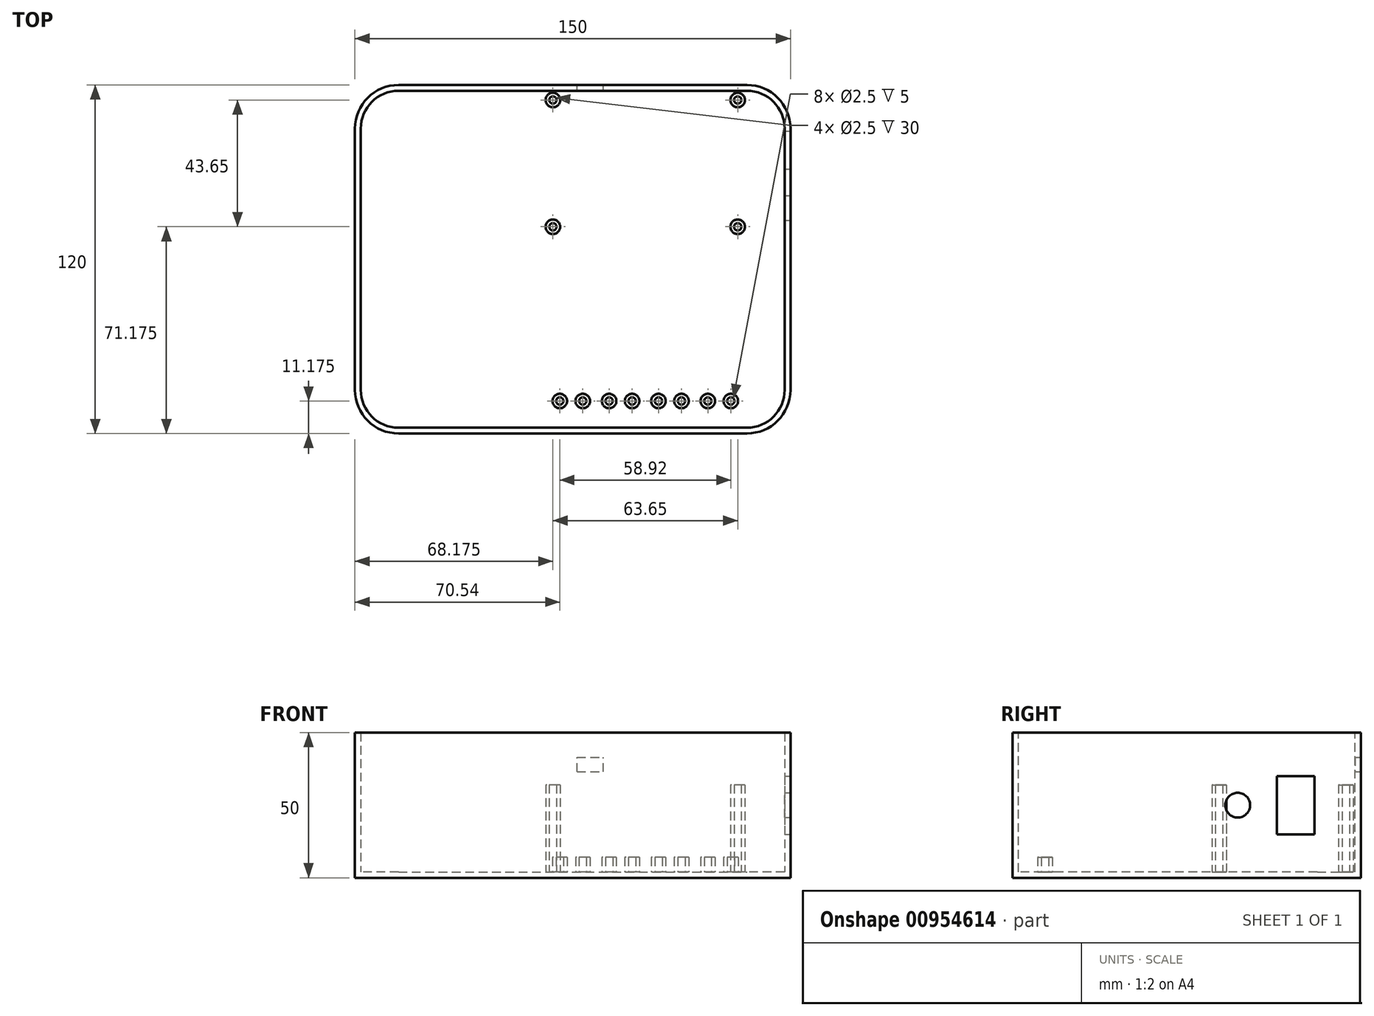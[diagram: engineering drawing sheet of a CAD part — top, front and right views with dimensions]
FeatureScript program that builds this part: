
annotation { "Feature Type Name" : "Feature", "Feature Type Description" : "" }
export const myFeature = defineFeature(function(context is Context, id is Id, definition is map)
    precondition{}
    {
        {
            var Q0;
            Q0=qCreatedBy(makeId("Top.planeOp"),FACE);
            var sketch = newSketch(context, id + "F0", { "sketchPlane" : qUnion([Q0])});
            skLineSegment(sketch, "E0.bottom", {"start": v(-60, 60) * mm, "end": v(60, 60) * mm});
            skLineSegment(sketch, "E0.top", {"start": v(-60, -60) * mm, "end": v(60, -60) * mm});
            skLineSegment(sketch, "E0.left", {"start": v(-75, 45) * mm, "end": v(-75, -45) * mm});
            skLineSegment(sketch, "E0.right", {"start": v(75, 45) * mm, "end": v(75, -45) * mm});
            skPoint(sketch, "E0.middle", {"position": v(0, 0) * mm});
            skPoint(sketch, "E1.visualSharp", {"position": v(-75, 60) * mm});
            skArc(sketch, "E1.filletArc", {"start": v(-60, 60) * mm, "mid": v(-70.6, 55.6) * mm, "end": v(-75, 45) * mm});
            skPoint(sketch, "E2.visualSharp", {"position": v(75, 60) * mm});
            skArc(sketch, "E2.filletArc", {"start": v(75, 45) * mm, "mid": v(70.6, 55.6) * mm, "end": v(60, 60) * mm});
            skPoint(sketch, "E3.visualSharp", {"position": v(75, -60) * mm});
            skArc(sketch, "E3.filletArc", {"start": v(60, -60) * mm, "mid": v(70.6, -55.6) * mm, "end": v(75, -45) * mm});
            skPoint(sketch, "E4.visualSharp", {"position": v(-75, -60) * mm});
            skArc(sketch, "E4.filletArc", {"start": v(-75, -45) * mm, "mid": v(-70.6, -55.6) * mm, "end": v(-60, -60) * mm});
            skSolve(sketch);
        }
        {
            var Q0;
            Q0=qSketchRegion(id+"F0",true);
            extrude(context, id + "F1", {"entities" : qUnion([Q0]), "depth" : 50 * mm, "offsetDistance" : 25 * mm});
        }
        {
            var Q0;
            Q0=makeQuery(id+"F1.opExtrude","CAP_FACE",FACE,{"disambiguationData":[OSD([sQuery(id+"F0.wireOp",EDGE,"E0.bottom"),sQuery(id+"F0.wireOp",EDGE,"E0.top"),sQuery(id+"F0.wireOp",EDGE,"E0.left"),sQuery(id+"F0.wireOp",EDGE,"E0.right"),sQuery(id+"F0.wireOp",EDGE,"E1.filletArc"),sQuery(id+"F0.wireOp",EDGE,"E2.filletArc"),sQuery(id+"F0.wireOp",EDGE,"E3.filletArc"),sQuery(id+"F0.wireOp",EDGE,"E4.filletArc")])],"isStart":false});
            shell(context, id + "F2", {"entities" : qUnion([Q0]), "thickness" : 2 * mm});
        }
        {
            var Q0;
            Q0=makeQuery(id+"F2.opShell","OFFSET_FACE",FACE,{"disambiguationData":[OSD([sQuery(id+"F0.wireOp",EDGE,"E0.bottom"),sQuery(id+"F0.wireOp",EDGE,"E0.top"),sQuery(id+"F0.wireOp",EDGE,"E0.left"),sQuery(id+"F0.wireOp",EDGE,"E0.right"),sQuery(id+"F0.wireOp",EDGE,"E1.filletArc"),sQuery(id+"F0.wireOp",EDGE,"E2.filletArc"),sQuery(id+"F0.wireOp",EDGE,"E3.filletArc"),sQuery(id+"F0.wireOp",EDGE,"E4.filletArc")])]});
            var sketch = newSketch(context, id + "F3", { "sketchPlane" : qUnion([Q0])});
            skCircle(sketch, "E5", {"center": v(-6.82, 54.82) * mm, "radius": 2.5 * mm});
            skCircle(sketch, "E6.MirrorC", {"center": v(-6.82, 11.17) * mm, "radius": 2.5 * mm});
            skCircle(sketch, "E7", {"center": v(56.83, 54.83) * mm, "radius": 2.5 * mm});
            skCircle(sketch, "E8.MirrorC", {"center": v(56.83, 11.17) * mm, "radius": 2.5 * mm});
            skCircle(sketch, "E9", {"center": v(-6.82, 54.82) * mm, "radius": 1.25 * mm});
            skCircle(sketch, "E10", {"center": v(56.83, 54.83) * mm, "radius": 1.25 * mm});
            skCircle(sketch, "E11", {"center": v(56.83, 11.17) * mm, "radius": 1.25 * mm});
            skCircle(sketch, "E12", {"center": v(-6.82, 11.17) * mm, "radius": 1.25 * mm});
            skSolve(sketch);
        }
        {
            var Q0;
            Q0=qSketchRegion(id+"F3",true);
            extrude(context, id + "F4", {"entities" : qUnion([Q0]), "operationType" : NewBodyOperationType.ADD, "depth" : 30 * mm, "offsetDistance" : 25 * mm});
        }
        {
            var Q0;
            Q0=makeQuery(id+"F1.opExtrude","SWEPT_FACE",FACE,{"disambiguationData":[OSD([sQuery(id+"F0.wireOp",EDGE,"E0.bottom")])]});
            var sketch = newSketch(context, id + "F5", { "sketchPlane" : qUnion([Q0])});
            skLineSegment(sketch, "E13.bottom", {"start": v(-1.5, 36.5) * mm, "end": v(-10.5, 36.5) * mm});
            skLineSegment(sketch, "E13.top", {"start": v(-1.5, 41.5) * mm, "end": v(-10.5, 41.5) * mm});
            skLineSegment(sketch, "E13.left", {"start": v(-1.5, 36.5) * mm, "end": v(-1.5, 41.5) * mm});
            skLineSegment(sketch, "E13.right", {"start": v(-10.5, 36.5) * mm, "end": v(-10.5, 41.5) * mm});
            skPoint(sketch, "E13.middle", {"position": v(-6, 39) * mm});
            skSolve(sketch);
        }
        {
            var Q0;
            Q0=qSketchRegion(id+"F5",true);
            extrude(context, id + "F6", {"entities" : qUnion([Q0]), "operationType" : NewBodyOperationType.REMOVE, "endBound" : BoundingType.UP_TO_NEXT, "oppositeDirection" : true, "depth" : 25 * mm, "offsetDistance" : 25 * mm});
        }
        {
            var Q0;
            Q0=makeQuery(id+"F1.opExtrude","CAP_FACE",FACE,{"disambiguationData":[OSD([sQuery(id+"F0.wireOp",EDGE,"E0.bottom"),sQuery(id+"F0.wireOp",EDGE,"E0.top"),sQuery(id+"F0.wireOp",EDGE,"E0.left"),sQuery(id+"F0.wireOp",EDGE,"E0.right"),sQuery(id+"F0.wireOp",EDGE,"E1.filletArc"),sQuery(id+"F0.wireOp",EDGE,"E2.filletArc"),sQuery(id+"F0.wireOp",EDGE,"E3.filletArc"),sQuery(id+"F0.wireOp",EDGE,"E4.filletArc")])],"isStart":false});
            var sketch = newSketch(context, id + "F7", { "sketchPlane" : qUnion([Q0])});
            skSolve(sketch);
        }
        {
            var Q0;
            Q0=makeQuery(id+"F1.opExtrude","SWEPT_FACE",FACE,{"disambiguationData":[OSD([sQuery(id+"F0.wireOp",EDGE,"E0.right")])]});
            var sketch = newSketch(context, id + "F8", { "sketchPlane" : qUnion([Q0])});
            skCircle(sketch, "E14", {"center": v(17.59, 25) * mm, "radius": 4.25 * mm});
            skLineSegment(sketch, "E15.bottom", {"start": v(44.09, 15) * mm, "end": v(31.09, 15) * mm});
            skLineSegment(sketch, "E15.top", {"start": v(44.09, 35) * mm, "end": v(31.09, 35) * mm});
            skLineSegment(sketch, "E15.left", {"start": v(44.09, 15) * mm, "end": v(44.09, 35) * mm});
            skLineSegment(sketch, "E15.right", {"start": v(31.09, 15) * mm, "end": v(31.09, 35) * mm});
            skPoint(sketch, "E15.middle", {"position": v(37.59, 25) * mm});
            skSolve(sketch);
        }
        {
            var Q0;
            Q0=qSketchRegion(id+"F8",true);
            extrude(context, id + "F9", {"entities" : qUnion([Q0]), "operationType" : NewBodyOperationType.REMOVE, "endBound" : BoundingType.UP_TO_NEXT, "oppositeDirection" : true, "depth" : 25 * mm, "offsetDistance" : 25 * mm});
        }
        {
            var Q0;
            {var subQ0=sQuery(id+"F0.wireOp",EDGE,"E0.right");var subQ1=sQuery(id+"F0.wireOp",EDGE,"E4.filletArc");var subQ2=sQuery(id+"F0.wireOp",EDGE,"E3.filletArc");var subQ3=sQuery(id+"F0.wireOp",EDGE,"E2.filletArc");var subQ4=sQuery(id+"F0.wireOp",EDGE,"E1.filletArc");var subQ5=sQuery(id+"F0.wireOp",EDGE,"E0.bottom");var subQ6=sQuery(id+"F0.wireOp",EDGE,"E0.top");var subQ7=sQuery(id+"F0.wireOp",EDGE,"E0.left");Q0=makeQuery(id+"F4.boolean.opBoolean","SPLIT",FACE,{"disambiguationData":[TD([makeQuery(id+"F2.opShell","OFFSET_FACE",FACE,{"disambiguationData":[OSD([subQ5])]})])],"derivedFrom":makeQuery(id+"F2.opShell","OFFSET_FACE",FACE,{"disambiguationData":[OSD([subQ5,subQ6,subQ7,subQ0,subQ4,subQ3,subQ2,subQ1])]})});}
            var sketch = newSketch(context, id + "F10", { "sketchPlane" : qUnion([Q0])});
            skCircle(sketch, "E16", {"center": v(-4.46, -48.83) * mm, "radius": 2.5 * mm});
            skCircle(sketch, "E17", {"center": v(-4.46, -48.83) * mm, "radius": 1.25 * mm});
            skCircle(sketch, "E18.0.1.0", {"center": v(3.46, -48.83) * mm, "radius": 2.5 * mm});
            skCircle(sketch, "E18.0.1.1", {"center": v(3.46, -48.83) * mm, "radius": 1.25 * mm});
            skLineSegment(sketch, "E18.direction2", {"start": v(-4.46, -48.83) * mm, "end": v(3.46, -48.83) * mm, "construction": true});
            skCircle(sketch, "E19.0.1.0", {"center": v(12.54, -48.83) * mm, "radius": 2.5 * mm});
            skCircle(sketch, "E19.0.1.1", {"center": v(12.54, -48.83) * mm, "radius": 1.25 * mm});
            skCircle(sketch, "E19.0.1.2", {"center": v(20.46, -48.83) * mm, "radius": 2.5 * mm});
            skCircle(sketch, "E19.0.1.3", {"center": v(20.46, -48.83) * mm, "radius": 1.25 * mm});
            skCircle(sketch, "E19.0.2.0", {"center": v(29.54, -48.83) * mm, "radius": 2.5 * mm});
            skCircle(sketch, "E19.0.2.1", {"center": v(29.54, -48.83) * mm, "radius": 1.25 * mm});
            skCircle(sketch, "E19.0.2.2", {"center": v(37.46, -48.83) * mm, "radius": 2.5 * mm});
            skCircle(sketch, "E19.0.2.3", {"center": v(37.46, -48.83) * mm, "radius": 1.25 * mm});
            skCircle(sketch, "E19.0.3.0", {"center": v(46.54, -48.83) * mm, "radius": 2.5 * mm});
            skCircle(sketch, "E19.0.3.1", {"center": v(46.54, -48.83) * mm, "radius": 1.25 * mm});
            skCircle(sketch, "E19.0.3.2", {"center": v(54.46, -48.83) * mm, "radius": 2.5 * mm});
            skCircle(sketch, "E19.0.3.3", {"center": v(54.46, -48.83) * mm, "radius": 1.25 * mm});
            skLineSegment(sketch, "E19.direction2", {"start": v(-4.46, -48.83) * mm, "end": v(12.54, -48.83) * mm, "construction": true});
            skLineSegment(sketch, "E20", {"start": v(-6.82, 11.17) * mm, "end": v(56.83, 11.17) * mm, "construction": true});
            skSolve(sketch);
        }
        {
            var Q0;
            Q0=qSketchRegion(id+"F10",true);
            extrude(context, id + "F11", {"entities" : qUnion([Q0]), "operationType" : NewBodyOperationType.ADD, "depth" : 5 * mm, "offsetDistance" : 25 * mm});
        }
    });
